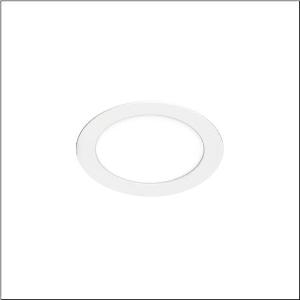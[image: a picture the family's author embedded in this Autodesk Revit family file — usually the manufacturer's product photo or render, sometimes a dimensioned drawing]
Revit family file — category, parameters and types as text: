
# Revit family: lunis_41_flat_51dr107fhca
name_source: partatom
category: Lighting Fixtures
units: mm (PartAtom-declared; Revit-internal decimal feet)

## family parameters
Cut with Voids When Loaded = No
Host = Face
Light Source = No
Part Type = Normal
Room Calculation Point = No
Round Connector Dimension = Use Diameter
Shared = No

## types (1)
- --- (1 x LED, 2160 lm, 22 W, 5700K)
    Apparent Load = 22 VA
    CIE Flux Codes = 49 80 96 100 100
    Color Rendering = 80
    Color Temperature = 5700K
    Default Elevation = 1800 mm
    Description = Lunis 41 Flat, downlight, light emission: direct distribution, LED rated luminous flux: 2.160lm, light colour: 840/857, control gear: ECG, mains connection: 230V, AC, 50/60Hz, housing, round, of aluminium, coated, traffic white (RAL 9016), diameter: 225mm, protection rating (complete): IP20, protection rating (on room side): IP44, insulation class (complete): insulation class II (safety insulation), certification: CE, permissible ambient temperature for indoor applications: -20..+40°C, packaging unit: 1 piece
    Height = 0 mm  [stored 0 ft]
    Lamp = 1 x LED
    Lamp Light Flux = 2160 lm
    Lamp Power = 22 W
    Lamp count = 1
    Length = 225 mm
    Luminous efficacy = 98 lm/W
    Manufacturer = Siteco
    ModVariant = No
    Model = 51DR107FHCA
    Mounting Place = Ceiling
    Mounting Type = Recessed
    Number of Poles = 1
    OnlyDefault = Yes
    Power Factor = 1
    Product Name = Lunis 41 Flat
    Product group = downlight
    ProductGroupID = 401
    Protection Class = Protection class II
    Protection Degree = IP 20
    RLX_Detail_Level = 1
    RLX_Emergency_Light_Flux = 0 lm
    RLX_Emergency_Type = 0
    RLX_Emergency_Type_DB = No
    RlxData = <blob elided: 22149 chars, md5=d1a3b04f>
    Socket = socket
    Standby Power = 0 W
    System Light Flux = 2160 lm
    System Power = 22 W
    Type Comments = factory setting: colour temperature 5700K
    Type Image = l_1340923.jpg
    URL = http://relux.com
    VarID = @adj_194589
    Voltage = 0 V
    Weight = 0.00 kg
    Width = 0 mm  [stored 0 ft]

note: [stored X ft] marks values corroborated as IEEE doubles in the binary element streams (Revit-internal decimal feet)

## geometry (parser evidence)
native form markers: Blend x4, Sweep x11
no freeform markers — native parametric forms only
